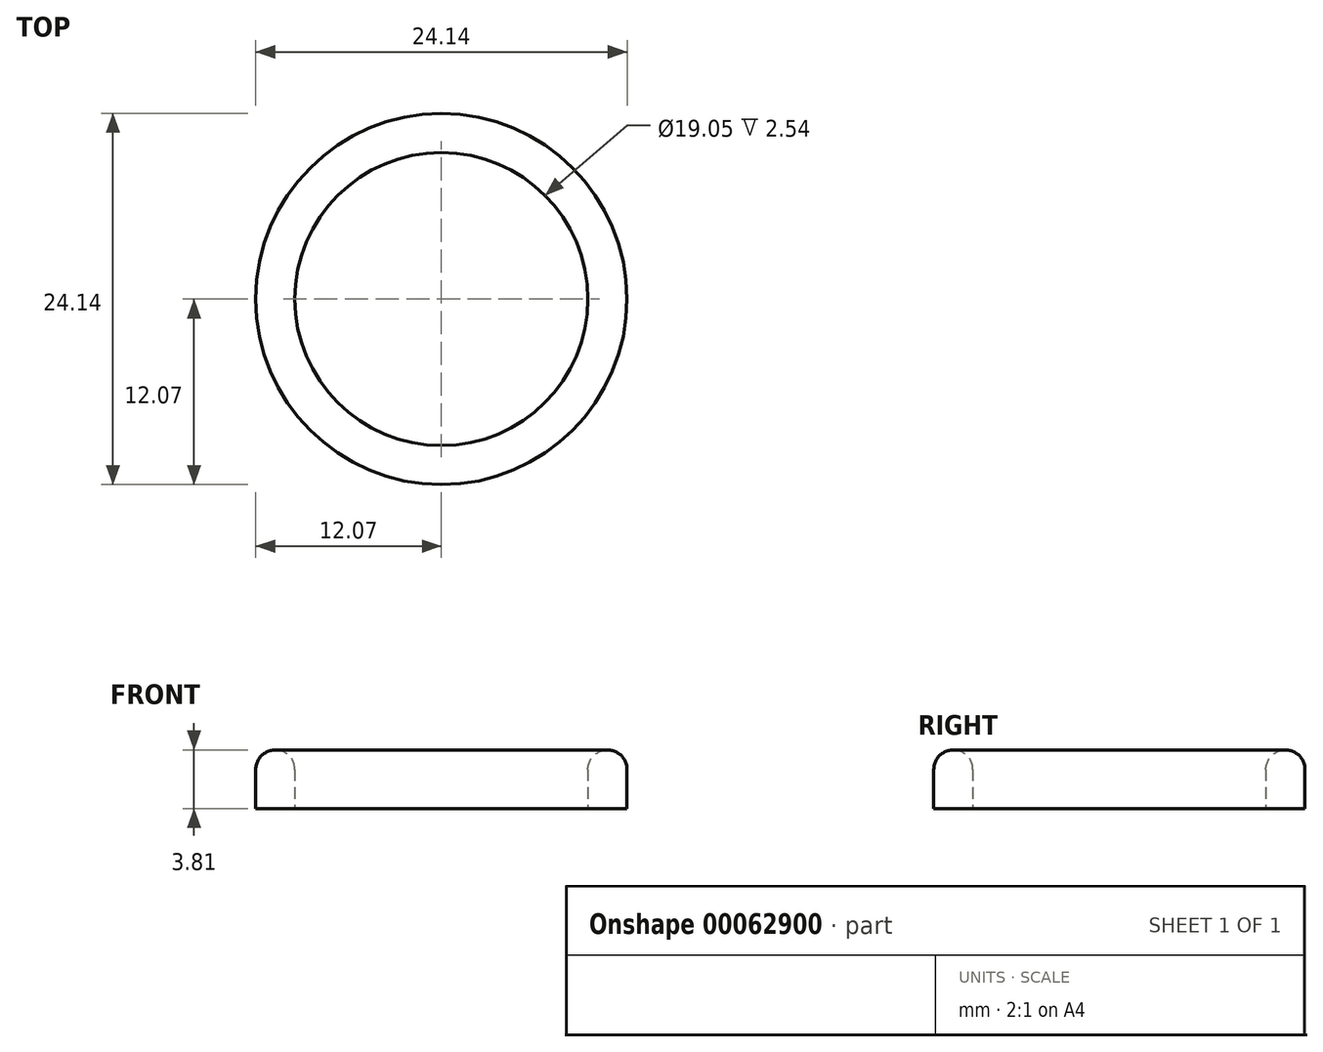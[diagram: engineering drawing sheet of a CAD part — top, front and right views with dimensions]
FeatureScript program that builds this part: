
annotation { "Feature Type Name" : "Feature", "Feature Type Description" : "" }
export const myFeature = defineFeature(function(context is Context, id is Id, definition is map)
    precondition{}
    {
        {
            var Q0;
            Q0=qCreatedBy(makeId("Top.planeOp"),FACE);
            var sketch = newSketch(context, id + "F0", { "sketchPlane" : qUnion([Q0])});
            skCircle(sketch, "E0", {"center": v(0, 0) * mm, "radius": 9.53 * mm});
            skCircle(sketch, "E1.0", {"center": v(0, 0) * mm, "radius": 12.07 * mm});
            skSolve(sketch);
        }
        {
            var Q0;
            Q0=makeQuery(id+"F0.imprint","IMPRINT",FACE,{"disambiguationData":[TD([[makeQuery(id+"F0.imprint","IMPRINT",EDGE,{"derivedFrom":sQuery(id+"F0.wireOp",EDGE,"E0")}),-1.0]])]});
            extrude(context, id + "F1", {"entities" : qUnion([Q0]), "depth" : 5.08 * mm});
        }
        {
            var Q0;
            Q0=makeQuery(id+"F1.opExtrude","CAP_EDGE",EDGE,{"disambiguationData":[OSD([sQuery(id+"F0.wireOp",EDGE,"E1.0")])],"isStart":false});
            fillet(context, id + "F2", {"entities" : qUnion([Q0]), "radius" : 2.54 * mm, "tangentPropagation" : true, "allowEdgeOverflow" : false});
        }
        {
            var Q0;
            Q0=makeQuery(id+"F2.opFillet","BLEND_EDGE",EDGE,{"blendedFrom":[makeQuery(id+"F1.opExtrude","CAP_EDGE",EDGE,{"disambiguationData":[OSD([sQuery(id+"F0.wireOp",EDGE,"E1.0")])],"isStart":false}),makeQuery(id+"F1.opExtrude","SWEPT_FACE",FACE,{"disambiguationData":[OSD([sQuery(id+"F0.wireOp",EDGE,"E0")])]})],"blendedInto":[makeQuery(id+"F1.opExtrude","SWEPT_FACE",FACE,{"disambiguationData":[OSD([sQuery(id+"F0.wireOp",EDGE,"E0")])]})]});
            fillet(context, id + "F3", {"entities" : qUnion([Q0]), "radius" : 1.27 * mm, "tangentPropagation" : true, "allowEdgeOverflow" : false});
        }
    });
